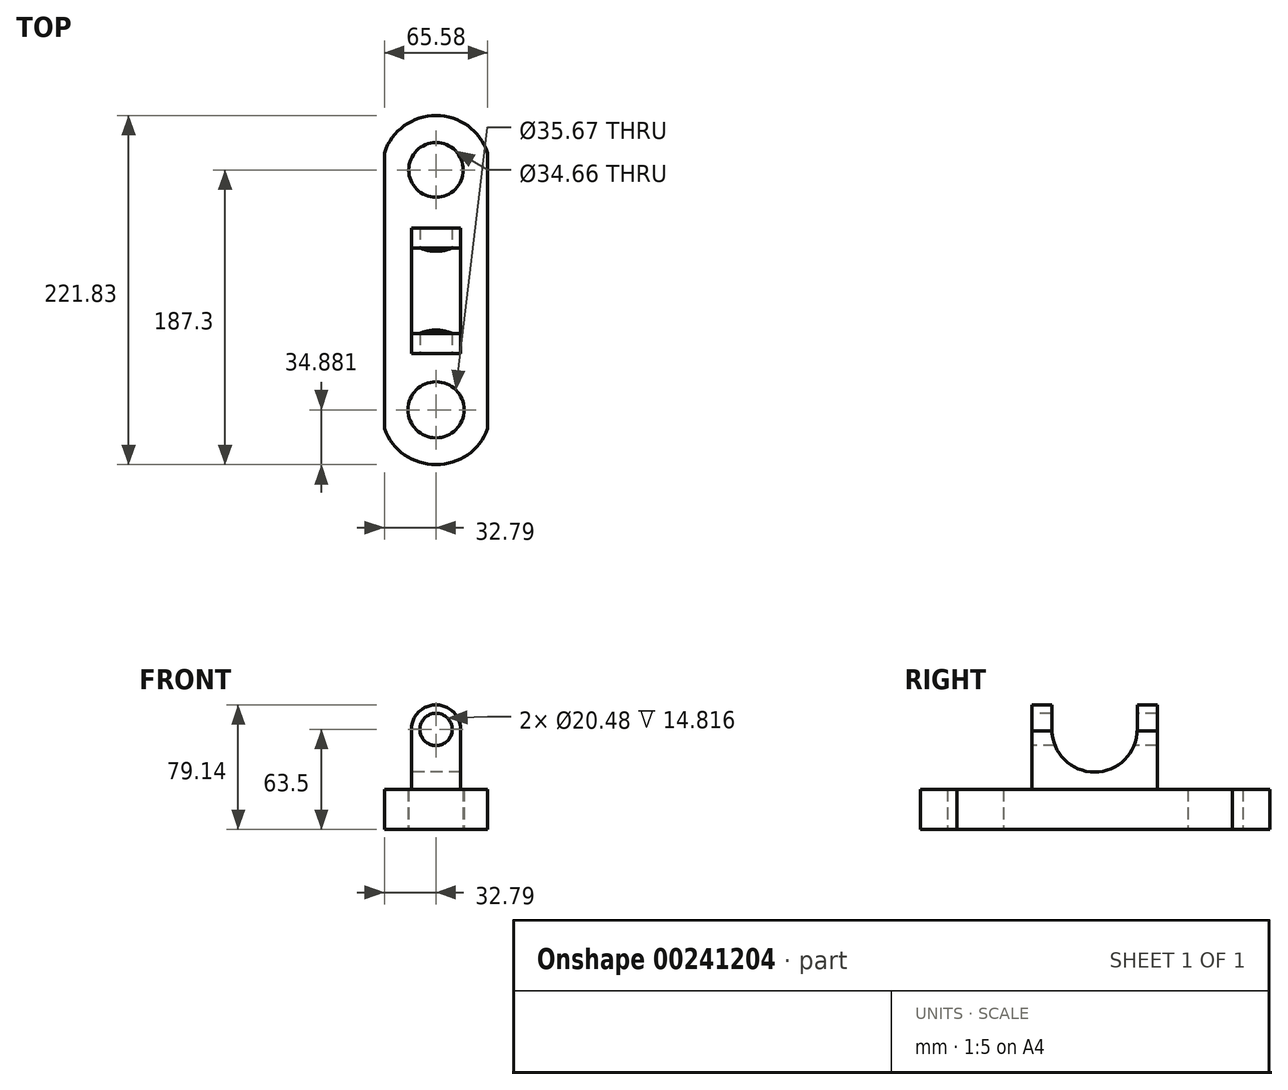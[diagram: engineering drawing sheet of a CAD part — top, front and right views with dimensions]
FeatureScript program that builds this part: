
annotation { "Feature Type Name" : "Feature", "Feature Type Description" : "" }
export const myFeature = defineFeature(function(context is Context, id is Id, definition is map)
    precondition{}
    {
        {
            var Q0;
            Q0=qCreatedBy(makeId("Top.planeOp"),FACE);
            var sketch = newSketch(context, id + "F0", { "sketchPlane" : qUnion([Q0])});
            skLineSegment(sketch, "E0.left", {"start": v(32.79, 87.56) * mm, "end": v(32.79, -87.56) * mm});
            skLineSegment(sketch, "E0.right", {"start": v(-32.79, 87.56) * mm, "end": v(-32.79, -87.56) * mm});
            skPoint(sketch, "E0.middle", {"position": v(0, 0) * mm});
            skArc(sketch, "E1", {"start": v(-32.79, -87.56) * mm, "mid": v(0, -110.55) * mm, "end": v(32.79, -87.56) * mm});
            skArc(sketch, "E2", {"start": v(32.79, 87.56) * mm, "mid": v(0, 111.28) * mm, "end": v(-32.79, 87.56) * mm});
            skCircle(sketch, "E3", {"center": v(0, -75.67) * mm, "radius": 17.84 * mm});
            skCircle(sketch, "E4", {"center": v(0, 76.75) * mm, "radius": 17.33 * mm});
            skSolve(sketch);
        }
        {
            var Q0;
            Q0=makeQuery(id+"F0.imprint","IMPRINT",FACE,{"disambiguationData":[TD([[makeQuery(id+"F0.imprint","IMPRINT",EDGE,{"derivedFrom":sQuery(id+"F0.wireOp",EDGE,"E0.left")}),-1.0]])]});
            extrude(context, id + "F1", {"entities" : qUnion([Q0]), "depth" : 25.4 * mm});
        }
        {
            var Q0;
            Q0=makeQuery(id+"F1.opExtrude","CAP_FACE",FACE,{"disambiguationData":[OSD([sQuery(id+"F0.wireOp",EDGE,"E0.left"),sQuery(id+"F0.wireOp",EDGE,"E0.right"),sQuery(id+"F0.wireOp",EDGE,"E1"),sQuery(id+"F0.wireOp",EDGE,"E2"),sQuery(id+"F0.wireOp",EDGE,"E3"),sQuery(id+"F0.wireOp",EDGE,"E4")])],"isStart":false});
            var sketch = newSketch(context, id + "F2", { "sketchPlane" : qUnion([Q0])});
            skLineSegment(sketch, "E5.bottom", {"start": v(15.61, 39.88) * mm, "end": v(-15.61, 39.88) * mm});
            skLineSegment(sketch, "E5.top", {"start": v(15.61, -39.88) * mm, "end": v(-15.61, -39.88) * mm});
            skLineSegment(sketch, "E5.left", {"start": v(15.61, 39.88) * mm, "end": v(15.61, -39.88) * mm});
            skLineSegment(sketch, "E5.right", {"start": v(-15.61, 39.88) * mm, "end": v(-15.61, -39.88) * mm});
            skPoint(sketch, "E5.middle", {"position": v(0, 0) * mm});
            skSolve(sketch);
        }
        {
            var Q0;
            Q0=makeQuery(id+"F2.imprint","IMPRINT",FACE,{"disambiguationData":[TD([[makeQuery(id+"F2.imprint","IMPRINT",EDGE,{"derivedFrom":sQuery(id+"F2.wireOp",EDGE,"E5.bottom")}),1.0]])]});
            extrude(context, id + "F3", {"entities" : qUnion([Q0]), "operationType" : NewBodyOperationType.ADD, "depth" : 38.1 * mm});
        }
        {
            var Q0;
            Q0=makeQuery(id+"F3.opExtrude","SWEPT_FACE",FACE,{"disambiguationData":[OSD([sQuery(id+"F2.wireOp",EDGE,"E5.right")])]});
            var sketch = newSketch(context, id + "F4", { "sketchPlane" : qUnion([Q0])});
            skCircle(sketch, "E6", {"center": v(0, 63.5) * mm, "radius": 27.07 * mm});
            skSolve(sketch);
        }
        {
            var Q0;
            {var subQ0=sQuery(id+"F4.wireOp",EDGE,"E6");var subQ1=makeQuery(id+"F3.opExtrude","CAP_EDGE",EDGE,{"disambiguationData":[OSD([sQuery(id+"F2.wireOp",EDGE,"E5.right")])],"isStart":false});var subQ2=makeQuery(id+"F4.imprint","INTERSECT",VERTEX,{"disambiguationData":[OD(0.0)],"derivedFrom":[subQ1,subQ0]});Q0=makeQuery(id+"F4.imprint","IMPRINT",FACE,{"disambiguationData":[TD([[makeQuery(id+"F4.imprint","IMPRINT",EDGE,{"disambiguationData":[TD([[subQ2,-1.0]])],"derivedFrom":subQ0}),1.0]])]});}
            extrude(context, id + "F5", {"entities" : qUnion([Q0]), "operationType" : NewBodyOperationType.REMOVE, "oppositeDirection" : true, "depth" : 50.8 * mm});
        }
        {
            var Q0;
            Q0=makeQuery(id+"F3.opExtrude","SWEPT_FACE",FACE,{"disambiguationData":[OSD([sQuery(id+"F2.wireOp",EDGE,"E5.bottom")])]});
            var sketch = newSketch(context, id + "F6", { "sketchPlane" : qUnion([Q0])});
            skCircle(sketch, "E7", {"center": v(0, 63.5) * mm, "radius": 15.64 * mm});
            skCircle(sketch, "E8", {"center": v(0, 63.5) * mm, "radius": 15.7 * mm});
            skSolve(sketch);
        }
        {
            var Q0;
            {var subQ1=sQuery(id+"F2.wireOp",EDGE,"E5.bottom");var subQ6=makeQuery(id+"F3.opExtrude","CAP_EDGE",EDGE,{"disambiguationData":[OSD([subQ1])],"isStart":false});Q0=makeQuery(id+"F6.imprint","IMPRINT",FACE,{"disambiguationData":[TD([[makeQuery(id+"F6.imprint","IMPRINT",EDGE,{"derivedFrom":subQ6}),1.0]])]});}
            extrude(context, id + "F7", {"entities" : qUnion([Q0]), "operationType" : NewBodyOperationType.ADD, "oppositeDirection" : true, "depth" : 12.7 * mm});
        }
        {
            var Q0;
            Q0=makeQuery(id+"F3.opExtrude","SWEPT_FACE",FACE,{"disambiguationData":[OSD([sQuery(id+"F2.wireOp",EDGE,"E5.top")])]});
            var sketch = newSketch(context, id + "F8", { "sketchPlane" : qUnion([Q0])});
            skCircle(sketch, "E9", {"center": v(0, 63.5) * mm, "radius": 15.64 * mm});
            skSolve(sketch);
        }
        {
            var Q0;
            {var subQ1=sQuery(id+"F2.wireOp",EDGE,"E5.top");var subQ6=makeQuery(id+"F3.opExtrude","CAP_EDGE",EDGE,{"disambiguationData":[OSD([subQ1])],"isStart":false});Q0=makeQuery(id+"F8.imprint","IMPRINT",FACE,{"disambiguationData":[TD([[makeQuery(id+"F8.imprint","IMPRINT",EDGE,{"derivedFrom":subQ6}),-1.0]])]});}
            extrude(context, id + "F9", {"entities" : qUnion([Q0]), "operationType" : NewBodyOperationType.ADD, "oppositeDirection" : true, "depth" : 12.7 * mm});
        }
        {
            var Q0;
            {var subQ0=sQuery(id+"F2.wireOp",EDGE,"E5.top");Q0=makeQuery(id+"F9.boolean.opBoolean","MERGE",FACE,{"derivedFrom":[makeQuery(id+"F3.opExtrude","SWEPT_FACE",FACE,{"disambiguationData":[OSD([subQ0])]}),makeQuery(id+"F9.opExtrude","CAP_FACE",FACE,{"disambiguationData":[OSD([subQ0,sQuery(id+"F2.wireOp",EDGE,"E5.left"),sQuery(id+"F2.wireOp",EDGE,"E5.right"),sQuery(id+"F8.wireOp",EDGE,"E9")])],"isStart":true})]});}
            var sketch = newSketch(context, id + "F10", { "sketchPlane" : qUnion([Q0])});
            skCircle(sketch, "E10", {"center": v(0, 63.5) * mm, "radius": 10.24 * mm});
            skSolve(sketch);
        }
        {
            var Q0;
            Q0=makeQuery(id+"F10.imprint","IMPRINT",FACE,{"disambiguationData":[TD([[makeQuery(id+"F10.imprint","IMPRINT",EDGE,{"derivedFrom":sQuery(id+"F10.wireOp",EDGE,"E10")}),1.0]])]});
            extrude(context, id + "F11", {"entities" : qUnion([Q0]), "operationType" : NewBodyOperationType.REMOVE, "oppositeDirection" : true, "depth" : 1270 * mm});
        }
    });
